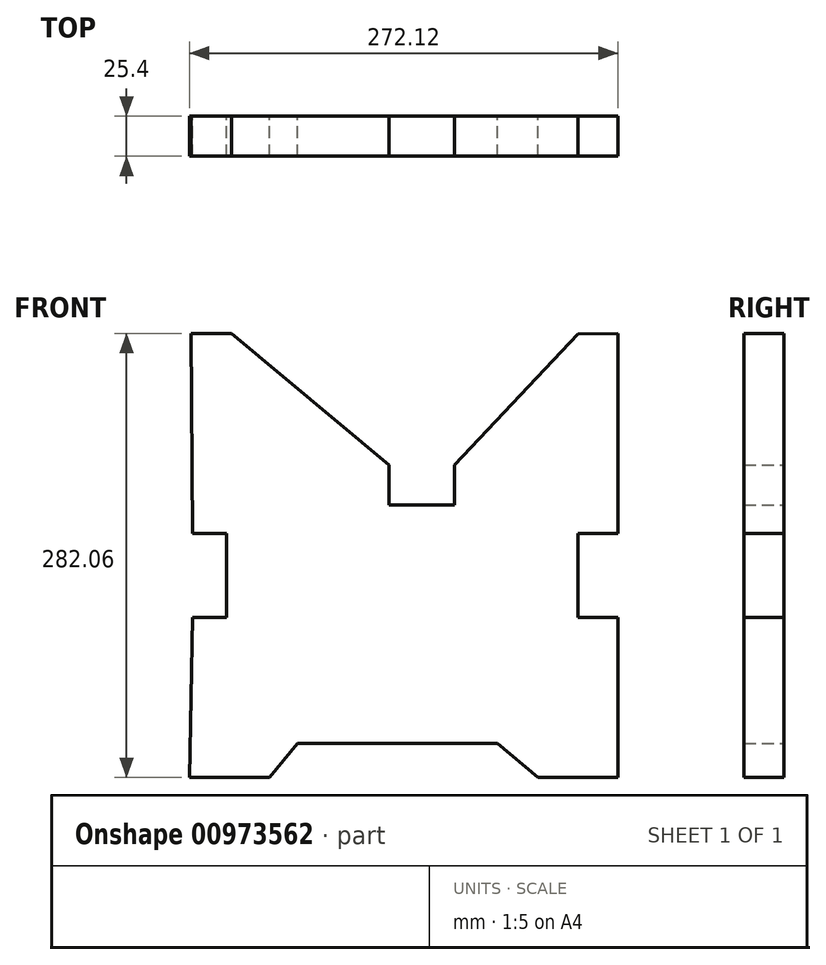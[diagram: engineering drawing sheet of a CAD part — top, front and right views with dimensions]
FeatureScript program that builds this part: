
annotation { "Feature Type Name" : "Feature", "Feature Type Description" : "" }
export const myFeature = defineFeature(function(context is Context, id is Id, definition is map)
    precondition{}
    {
        {
            var Q0;
            Q0=qCreatedBy(makeId("Front.planeOp"),FACE);
            var sketch = newSketch(context, id + "F0", { "sketchPlane" : qUnion([Q0])});
            skLineSegment(sketch, "E0", {"start": v(-167.14, 180.48) * mm, "end": v(-141.74, 180.48) * mm});
            skLineSegment(sketch, "E1", {"start": v(-141.74, 180.48) * mm, "end": v(-41.66, 96.95) * mm});
            skLineSegment(sketch, "E2", {"start": v(-41.66, 96.95) * mm, "end": v(-41.66, 71.55) * mm});
            skLineSegment(sketch, "E3", {"start": v(-41.66, 71.55) * mm, "end": v(0, 71.55) * mm});
            skLineSegment(sketch, "E4", {"start": v(0, 71.55) * mm, "end": v(0, 96.95) * mm});
            skLineSegment(sketch, "E5", {"start": v(0, 96.95) * mm, "end": v(78.47, 180.06) * mm});
            skLineSegment(sketch, "E6", {"start": v(78.47, 180.06) * mm, "end": v(103.86, 180.48) * mm});
            skLineSegment(sketch, "E7", {"start": v(103.86, 180.48) * mm, "end": v(103.86, 53.48) * mm});
            skLineSegment(sketch, "E8", {"start": v(103.86, 53.48) * mm, "end": v(78.47, 53.48) * mm});
            skLineSegment(sketch, "E9", {"start": v(78.47, 53.48) * mm, "end": v(78.47, 0.02) * mm});
            skLineSegment(sketch, "E10", {"start": v(78.47, 0.02) * mm, "end": v(103.86, 0.02) * mm});
            skLineSegment(sketch, "E11", {"start": v(103.86, 0.02) * mm, "end": v(103.86, -101.58) * mm});
            skLineSegment(sketch, "E12", {"start": v(103.86, -101.58) * mm, "end": v(53.06, -101.58) * mm});
            skLineSegment(sketch, "E13", {"start": v(53.06, -101.58) * mm, "end": v(27.41, -80.17) * mm});
            skLineSegment(sketch, "E14", {"start": v(27.41, -80.17) * mm, "end": v(-99.59, -80.17) * mm});
            skLineSegment(sketch, "E15", {"start": v(-99.59, -80.17) * mm, "end": v(-117.46, -101.58) * mm});
            skLineSegment(sketch, "E16", {"start": v(-117.46, -101.58) * mm, "end": v(-168.26, -101.58) * mm});
            skLineSegment(sketch, "E17", {"start": v(-168.26, 0.02) * mm, "end": v(-166, 0.02) * mm});
            skLineSegment(sketch, "E18", {"start": v(-166.35, 53.48) * mm, "end": v(-144.7, 53.48) * mm});
            skLineSegment(sketch, "E19", {"start": v(-144.7, 53.48) * mm, "end": v(-144.7, 0) * mm});
            skLineSegment(sketch, "E20", {"start": v(-144.7, 0) * mm, "end": v(-166.35, 0) * mm});
            skLineSegment(sketch, "E21", {"start": v(-166.35, 0) * mm, "end": v(-168.26, -101.58) * mm});
            skLineSegment(sketch, "E22", {"start": v(-167.14, 180.48) * mm, "end": v(-166.35, 53.48) * mm});
            skSolve(sketch);
        }
        {
            var Q0;
            Q0=makeQuery(id+"F0.imprint","IMPRINT",FACE,{"disambiguationData":[TD([[makeQuery(id+"F0.imprint","IMPRINT",EDGE,{"derivedFrom":sQuery(id+"F0.wireOp",EDGE,"E0")}),-1.0]])]});
            extrude(context, id + "F1", {"entities" : qUnion([Q0]), "depth" : 25.4 * mm, "offsetDistance" : 25.4 * mm});
        }
    });
